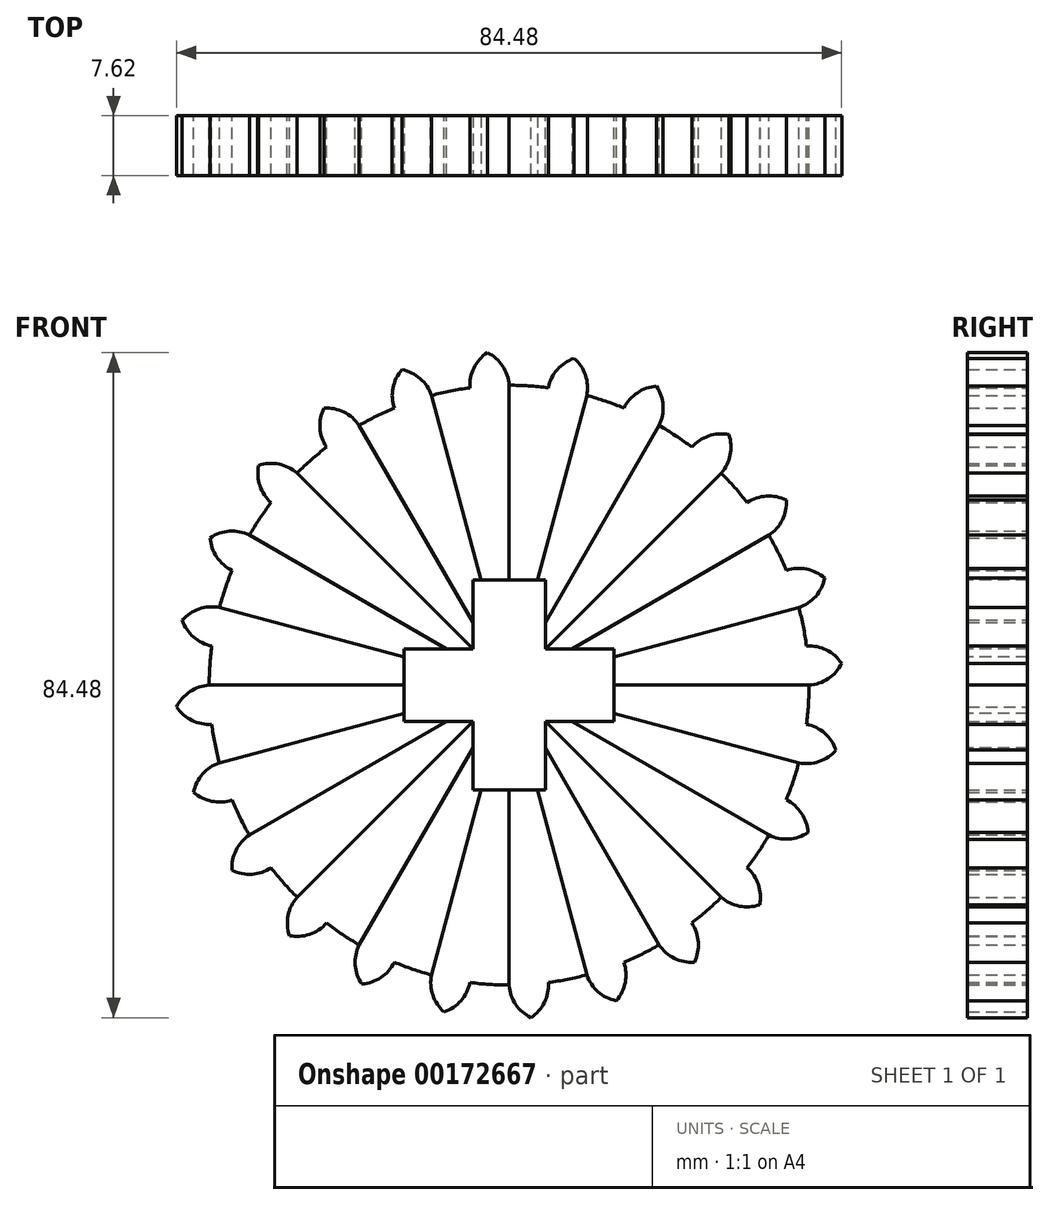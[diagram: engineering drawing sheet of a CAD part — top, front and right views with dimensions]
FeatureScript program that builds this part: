
annotation { "Feature Type Name" : "Feature", "Feature Type Description" : "" }
export const myFeature = defineFeature(function(context is Context, id is Id, definition is map)
    precondition{}
    {
        {
            var Q0;
            Q0=qCreatedBy(makeId("Front.planeOp"),FACE);
            var sketch = newSketch(context, id + "F0", { "sketchPlane" : qUnion([Q0])});
            skLineSegment(sketch, "E0", {"start": v(0, 0) * mm, "end": v(38.1, 0) * mm});
            skLineSegment(sketch, "E1", {"start": v(0, 0) * mm, "end": v(36.8, 9.86) * mm});
            skArc(sketch, "E2", {"start": v(38.1, 0) * mm, "mid": v(37.77, 4.97) * mm, "end": v(36.8, 9.86) * mm});
            skArc(sketch, "E3.trimOffspring", {"start": v(38.1, 0) * mm, "mid": v(40.54, 0.83) * mm, "end": v(42.24, 2.77) * mm});
            skArc(sketch, "E4.trimOffspring", {"start": v(42.24, 2.77) * mm, "mid": v(40.3, 4.47) * mm, "end": v(37.77, 4.97) * mm});
            skLineSegment(sketch, "E5", {"start": v(0, 0) * mm, "end": v(37.77, 4.97) * mm, "construction": true});
            skLineSegment(sketch, "E6", {"start": v(0, 0) * mm, "end": v(42.24, 2.77) * mm, "construction": true});
            skSolve(sketch);
        }
        {
            var Q0;
            {var subQ0=sQuery(id+"F0.wireOp",EDGE,"E3.trimOffspring");Q0=makeQuery(id+"F0.imprint","IMPRINT",FACE,{"disambiguationData":[TD([[makeQuery(id+"F0.imprint","IMPRINT",EDGE,{"derivedFrom":subQ0}),1.0]])]});}
            var Q1;
            {var subQ0=sQuery(id+"F0.wireOp",EDGE,"E0");Q1=makeQuery(id+"F0.imprint","IMPRINT",FACE,{"disambiguationData":[TD([[makeQuery(id+"F0.imprint","IMPRINT",EDGE,{"derivedFrom":subQ0}),1.0]])]});}
            extrude(context, id + "F1", {"entities" : qUnion([Q0, Q1]), "depth" : 7.62 * mm});
        }
        {
            var Q0;
            Q0=makeQuery(id+"F1.opExtrude","SWEPT_BODY",BODY,{"disambiguationData":[OSD([sQuery(id+"F0.wireOp",EDGE,"E0"),sQuery(id+"F0.wireOp",EDGE,"E1"),sQuery(id+"F0.wireOp",EDGE,"E2"),sQuery(id+"F0.wireOp",EDGE,"E3.trimOffspring"),sQuery(id+"F0.wireOp",EDGE,"E4.trimOffspring")])]});
            var Q1;
            Q1=makeQuery(id+"F1.opExtrude","SWEPT_EDGE",EDGE,{"disambiguationData":[OSD([sQuery(id+"F0.wireOp",EDGE,"E0"),sQuery(id+"F0.wireOp",EDGE,"E1")])]});
            circularPattern(context, id + "F2", {"entities" : qUnion([Q0]), "axis" : qUnion([Q1]), "angle" : 15 * degree, "instanceCount" : 24});
        }
        {
            var Q0;
            Q0=qCreatedBy(makeId("Front.planeOp"),FACE);
            var sketch = newSketch(context, id + "F3", { "sketchPlane" : qUnion([Q0])});
            skLineSegment(sketch, "E7.bottom", {"start": v(13.34, 4.61) * mm, "end": v(-13.34, 4.61) * mm});
            skLineSegment(sketch, "E7.top", {"start": v(13.34, -4.61) * mm, "end": v(-13.34, -4.61) * mm});
            skLineSegment(sketch, "E7.left", {"start": v(13.34, 4.61) * mm, "end": v(13.34, -4.61) * mm});
            skLineSegment(sketch, "E7.right", {"start": v(-13.34, 4.61) * mm, "end": v(-13.34, -4.61) * mm});
            skPoint(sketch, "E7.middle", {"position": v(0, 0) * mm});
            skLineSegment(sketch, "E8.bottom", {"start": v(4.61, 13.34) * mm, "end": v(-4.61, 13.34) * mm});
            skLineSegment(sketch, "E8.top", {"start": v(4.61, -13.34) * mm, "end": v(-4.61, -13.34) * mm});
            skLineSegment(sketch, "E8.left", {"start": v(4.61, 13.34) * mm, "end": v(4.61, -13.34) * mm});
            skLineSegment(sketch, "E8.right", {"start": v(-4.61, 13.34) * mm, "end": v(-4.61, -13.34) * mm});
            skSolve(sketch);
        }
        {
            var Q0;
            Q0 = qSketchRegion(id + "F3", true);
            extrude(context, id + "F4", {"entities" : qUnion([Q0]), "operationType" : NewBodyOperationType.REMOVE, "depth" : 25.4 * mm});
        }
    });
